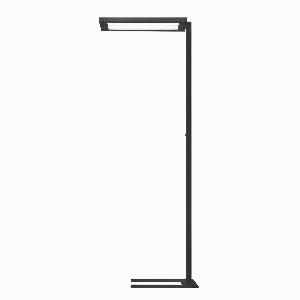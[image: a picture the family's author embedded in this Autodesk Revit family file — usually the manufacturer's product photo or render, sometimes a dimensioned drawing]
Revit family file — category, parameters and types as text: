
# Revit family: lavigo_core_-_dps_12500_840_r_g1_sw_00812433_b0a5
name_source: partatom
category: Lighting Fixtures
units: mm (PartAtom-declared; Revit-internal decimal feet)

## family parameters
Cut with Voids When Loaded = No
Host = Face
Light Source = No
Part Type = Normal
Room Calculation Point = No
Round Connector Dimension = Use Diameter
Shared = No

## types (1)
- LAVIGO.core - DPS 12500/840/R/G1/SW (1 x LED, 12400 lm, 4000K)
    Apparent Load = 85 VA
    Approval mark = CE
    CIE Flux Codes = 58 87 97 17 100
    Color Rendering = 80-89
    Color Temperature = 4000K
    Control Gear = Electronic ballast
    Default Elevation = 1800 mm
    Description = DPS 12500/840/R/G1|Free-standing luminaire|light source: LED Cold white   |work equipment: Electronic ballast DALI|connected load: 220-240 V, 50/60 Hz|Power consumption: approx. 85 W|standby: approx. 0,30|power factor: approx. 0,973|luminous flux: 12400 lm|luminous efficacy: 145 lm/W|light distribution: Direct/indirect|direct ratio: approx. 17 %|color rendering index (CRI): >= 80|chromaticity tolerance:  3 SDCM|technology: Presence and daylight sensor control (PIR)|operation: Rocker switch|luminaire body|material: Steel/plastic|surface: Painted|colour: Black|lamp cover: Polycarbonate (PC), Clear|tubular section|material: Steel tube|surface: Painted|Form: Tubular section upright|colour of tubular section: Black|luminaire base|Form: C-form flat|weight (net): approx. 14.7 kg|mains lead: 3.00 m Mains plug CEE 7/VII|Fastening: Floor standing base|decorative contrast side parts: Black|glare control: Prism aperture|luminance(L65): <= 3000 cd/m|unified glare rating(4H 8H): <=  16|special features: Luminaire head detachable, Direct and indirect light switchable together, Flicker-free, Integrated light and presence sensor PIR, Motion sensor time-out of 15mins~|Approval mark: US~B_0014~VDE - ENEC|
    Frequency = 50 Hz, 60 Hz
    Height = 36 mm
    Lamp = 1 x LED
    Lamp Light Flux = 12400 lm
    Lamp count = 1
    Length = 675 mm
    Luminous efficacy = 146 lm/W
    Manufacturer = Waldmann
    ModVariant = No
    Model = 00812433
    Mounting Place = Floor
    Mounting Type = Freestanding
    Number of Poles = 1
    OnlyDefault = Yes
    Power Factor = 1
    Product Name = LAVIGO.core - DPS 12500/840/R/G1/SW
    Product group = Free standing luminaire
    ProductGroupID = 13
    Protection Class = Protection class I
    Protection Degree = IP 20
    RLX_Detail_Level = 1
    RLX_Emergency_Light_Flux = 0 lm
    RLX_Emergency_Type = 0
    RLX_Emergency_Type_DB = No
    RlxData = <blob elided: 33385 chars, md5=54ce7435>
    Socket = socket
    Standby Power = 0 W
    System Light Flux = 12400 lm
    System Power = 85 W
    Type Comments = Product without accessories
    Type Image = 121805000-00755032_sw.jpg
    URL = http://relux.com
    VarID = ---
    Voltage = 230 V
    Voltage Range = 220-240 V
    Weight = 0.00 kg
    Width = 320 mm

## geometry (parser evidence)
native form markers: Blend x4, Sweep x16
no freeform markers — native parametric forms only
